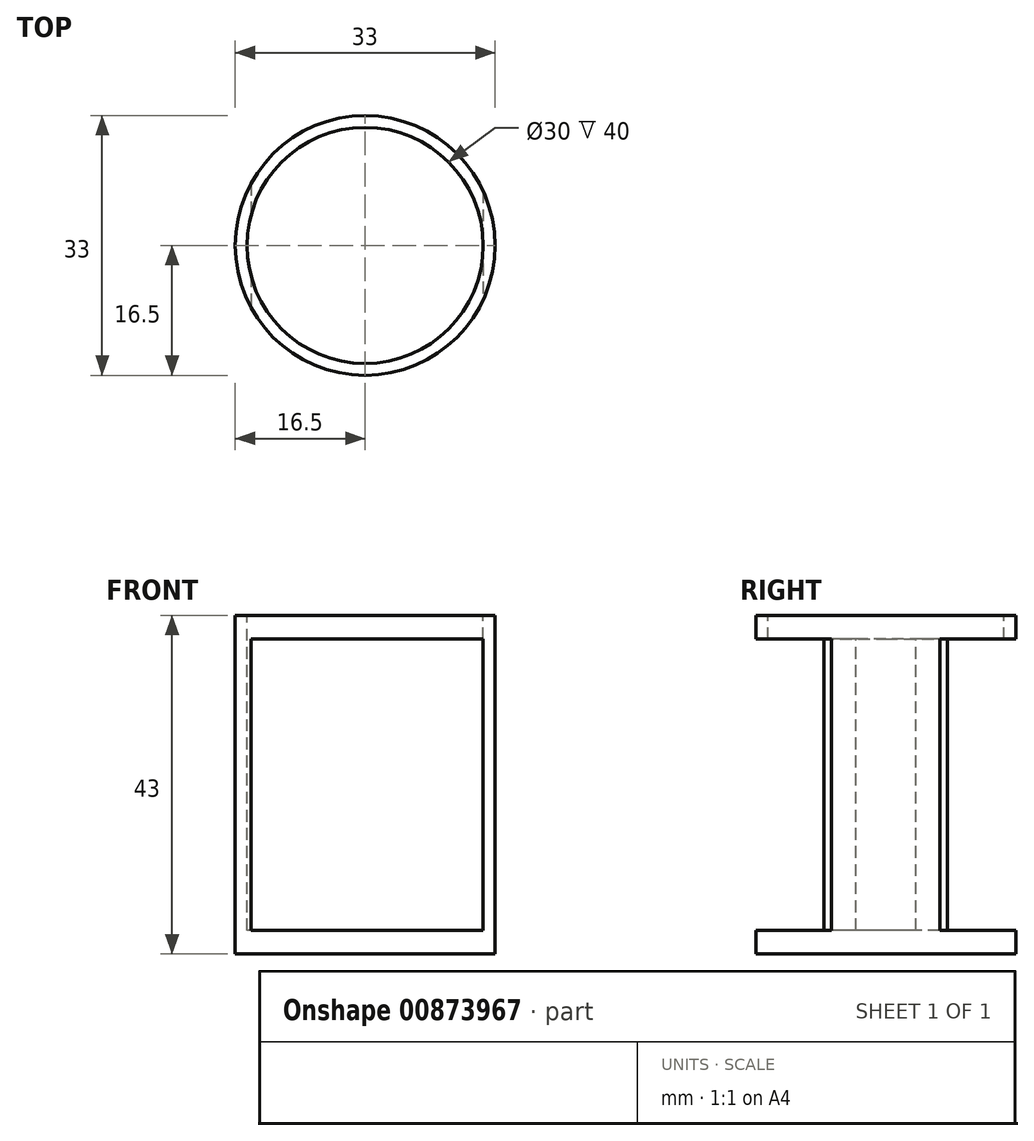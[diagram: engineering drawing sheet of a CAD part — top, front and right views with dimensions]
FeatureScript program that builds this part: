
annotation { "Feature Type Name" : "Feature", "Feature Type Description" : "" }
export const myFeature = defineFeature(function(context is Context, id is Id, definition is map)
    precondition{}
    {
        {
            var Q0;
            Q0=qCreatedBy(makeId("Top.planeOp"),FACE);
            var sketch = newSketch(context, id + "F0", { "sketchPlane" : qUnion([Q0])});
            skCircle(sketch, "E0", {"center": v(0, 0) * mm, "radius": 16.5 * mm});
            skSolve(sketch);
        }
        {
            var Q0;
            Q0 = qSketchRegion(id + "F0", true);
            extrude(context, id + "F1", {"entities" : qUnion([Q0]), "depth" : 43 * mm, "offsetDistance" : 25 * mm});
        }
        {
            var Q0;
            Q0=makeQuery(id+"F1.opExtrude","CAP_FACE",FACE,{"disambiguationData":[OSD([sQuery(id+"F0.wireOp",EDGE,"E0")])],"isStart":false});
            var sketch = newSketch(context, id + "F2", { "sketchPlane" : qUnion([Q0])});
            skCircle(sketch, "E1", {"center": v(0, 0) * mm, "radius": 15 * mm});
            skSolve(sketch);
        }
        {
            var Q0;
            Q0 = qSketchRegion(id + "F2", true);
            extrude(context, id + "F3", {"entities" : qUnion([Q0]), "operationType" : NewBodyOperationType.REMOVE, "oppositeDirection" : true, "depth" : 40 * mm, "offsetDistance" : 25 * mm});
        }
        {
            var Q0;
            Q0=qCreatedBy(makeId("Front.planeOp"),FACE);
            cPlane(context, id + "F4", {"entities" : qUnion([Q0]), "cplaneType" : CPlaneType.OFFSET, "offset" : 50 * mm, "width" : 150 * mm, "height" : 150 * mm});
        }
        {
            var Q0;
            Q0=qCreatedBy(id+"F4.planeOp",FACE);
            var sketch = newSketch(context, id + "F5", { "sketchPlane" : qUnion([Q0])});
            skPoint(sketch, "E2", {"position": v(0, 0) * mm});
            skPoint(sketch, "E3", {"position": v(15, 0) * mm});
            skPoint(sketch, "E4", {"position": v(15, 3) * mm});
            skLineSegment(sketch, "E5.bottom", {"start": v(15, 3) * mm, "end": v(-14.5, 3) * mm});
            skLineSegment(sketch, "E5.top", {"start": v(15, 40) * mm, "end": v(-14.5, 40) * mm});
            skLineSegment(sketch, "E5.left", {"start": v(15, 3) * mm, "end": v(15, 40) * mm});
            skLineSegment(sketch, "E5.right", {"start": v(-14.5, 3) * mm, "end": v(-14.5, 40) * mm});
            skSolve(sketch);
        }
        {
            var Q0;
            Q0 = qSketchRegion(id + "F5", true);
            extrude(context, id + "F6", {"entities" : qUnion([Q0]), "operationType" : NewBodyOperationType.REMOVE, "endBound" : BoundingType.THROUGH_ALL, "oppositeDirection" : true, "depth" : 25 * mm, "offsetDistance" : 25 * mm});
        }
    });
